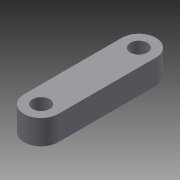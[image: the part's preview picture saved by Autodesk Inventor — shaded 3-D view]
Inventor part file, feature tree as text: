
AUTODESK INVENTOR PART (.ipt)
format: ipt  version: 2015 (Build 190159000, 159)  size: 92,672 bytes
history: native  units: mm
features: extrude x2, sketch x2
ambient origin geometry x8: Origin, YZ Plane, XZ Plane, XY Plane, X Axis, Y Axis, Z Axis, Center Point
bodies: Solid1 (feature_tree)
feature tree (4):
  extrude  "Extrusion1"  Depth=20.0mm
  extrude  "Extrusion2"  Depth=5.0mm TaperAngle=0.0deg
  sketch  "Sketch1"  dims[d0=7.0mm d1=20.0mm]
  sketch  "Sketch2"  dims[d2=7.0mm d3=5.0mm d4=0.0mm d5=3.5mm d6=3.5mm d7=5.0mm d8=0.0mm]
